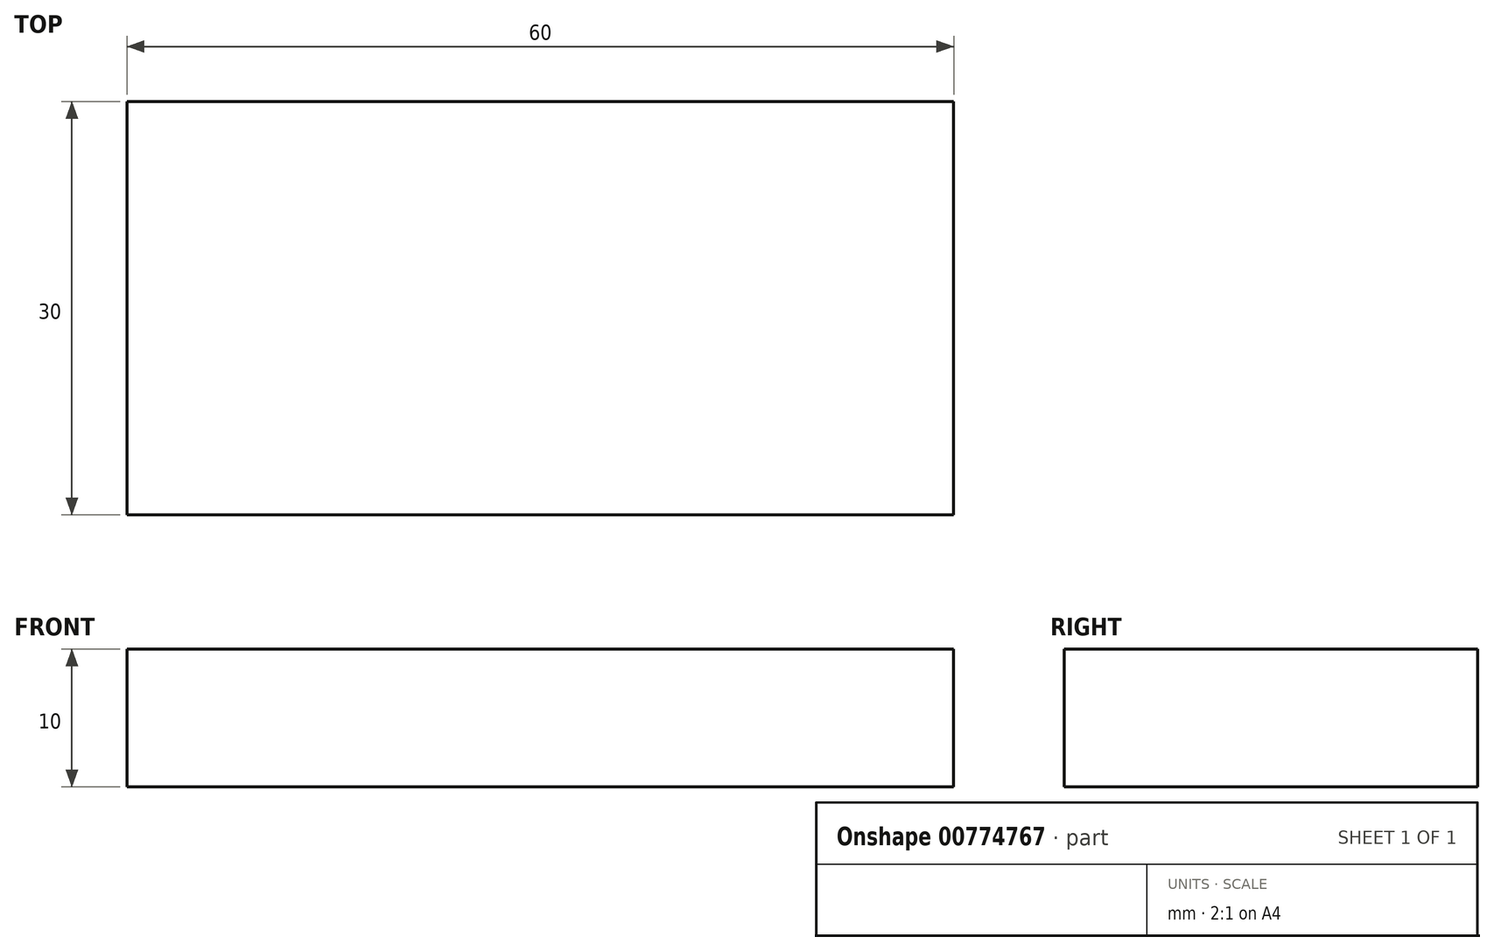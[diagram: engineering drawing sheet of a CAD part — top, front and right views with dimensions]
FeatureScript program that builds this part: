
annotation { "Feature Type Name" : "Feature", "Feature Type Description" : "" }
export const myFeature = defineFeature(function(context is Context, id is Id, definition is map)
    precondition{}
    {
        {
            var Q0;
            Q0=qCreatedBy(makeId("Top.planeOp"),FACE);
            var sketch = newSketch(context, id + "F0", { "sketchPlane" : qUnion([Q0])});
            skLineSegment(sketch, "E0.bottom", {"start": v(6.9, 6.72) * mm, "end": v(-53.1, 6.72) * mm});
            skLineSegment(sketch, "E0.top", {"start": v(6.9, 36.72) * mm, "end": v(-53.1, 36.72) * mm});
            skLineSegment(sketch, "E0.left", {"start": v(6.9, 6.72) * mm, "end": v(6.9, 36.72) * mm});
            skLineSegment(sketch, "E0.right", {"start": v(-53.1, 6.72) * mm, "end": v(-53.1, 36.72) * mm});
            skPoint(sketch, "E0.middle", {"position": v(-23.1, 21.72) * mm});
            skSolve(sketch);
        }
        {
            var Q0;
            Q0=makeQuery(id+"F0.imprint","IMPRINT",FACE,{"disambiguationData":[TD([[makeQuery(id+"F0.imprint","IMPRINT",EDGE,{"derivedFrom":sQuery(id+"F0.wireOp",EDGE,"E0.bottom")}),-1.0]])]});
            extrude(context, id + "F1", {"entities" : qUnion([Q0]), "depth" : 10 * mm, "offsetDistance" : 25 * mm});
        }
    });
